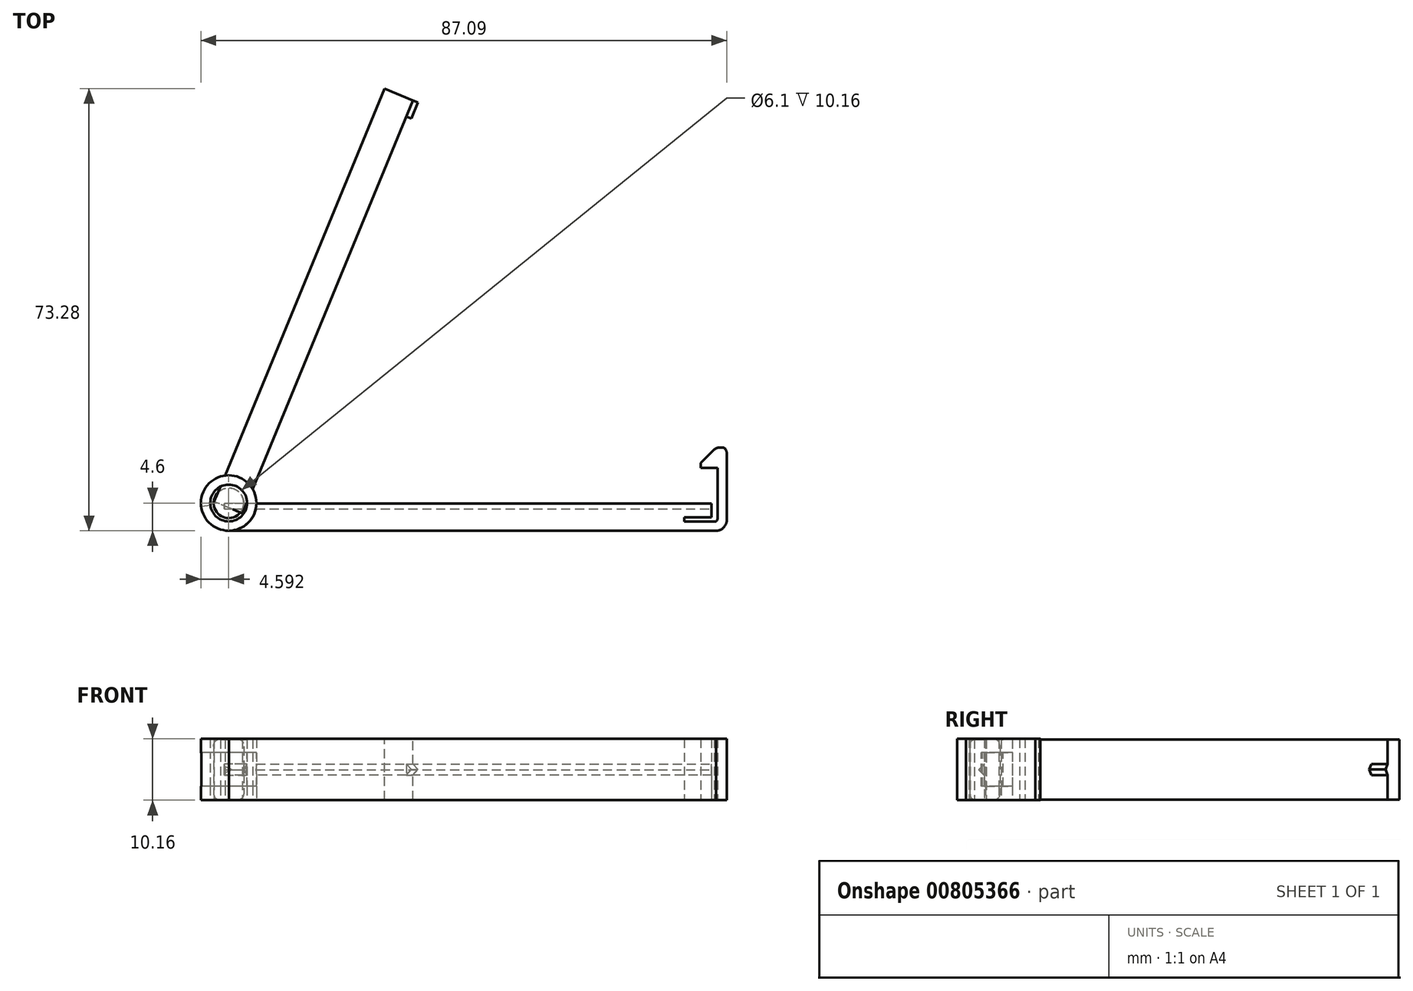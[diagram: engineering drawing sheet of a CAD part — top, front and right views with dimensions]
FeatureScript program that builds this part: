
annotation { "Feature Type Name" : "Feature", "Feature Type Description" : "" }
export const myFeature = defineFeature(function(context is Context, id is Id, definition is map)
    precondition{}
    {
        {
            assignVariable(context, id + "F0", {"name" : "length", "anyValue" : 1});
        }
        {
            var Q0;
            Q0=qCreatedBy(makeId("Top.planeOp"),FACE);
            var sketch = newSketch(context, id + "F1", { "sketchPlane" : qUnion([Q0])});
            skPoint(sketch, "E0", {"position": v(-38.94, -27.75) * mm});
            skCircle(sketch, "E1", {"center": v(-38.94, -27.75) * mm, "radius": 2.5 * mm});
            skLineSegment(sketch, "E2", {"start": v(-40.72, -25.98) * mm, "end": v(-38.24, -19.97) * mm});
            skLineSegment(sketch, "E3", {"start": v(14.08, 32.35) * mm, "end": v(17.62, 28.81) * mm});
            skLineSegment(sketch, "E4", {"start": v(-34.78, -23.44) * mm, "end": v(-33.99, -24.23) * mm});
            skLineSegment(sketch, "E5", {"start": v(-33.99, -24.23) * mm, "end": v(18.32, 28.1) * mm});
            skLineSegment(sketch, "E6", {"start": v(18.32, 28.1) * mm, "end": v(17.62, 28.81) * mm});
            skLineSegment(sketch, "E7", {"start": v(-40.72, -25.98) * mm, "end": v(-38.94, -27.75) * mm});
            skLineSegment(sketch, "E8", {"start": v(-37.25, -25.9) * mm, "end": v(-38.94, -27.75) * mm});
            skLineSegment(sketch, "E9", {"start": v(-38.24, -19.97) * mm, "end": v(-34.78, -23.44) * mm});
            skPoint(sketch, "E10", {"position": v(-38.24, -19.97) * mm});
            skLineSegment(sketch, "E11", {"start": v(-38.24, -19.97) * mm, "end": v(-38.24, -19.97) * mm});
            skLineSegment(sketch, "E12", {"start": v(-38.24, -19.97) * mm, "end": v(14.08, 32.35) * mm});
            skLineSegment(sketch, "E13", {"start": v(-37.25, -25.9) * mm, "end": v(-34.78, -23.44) * mm});
            skLineSegment(sketch, "E14", {"start": v(-34.78, -23.44) * mm, "end": v(17.62, 28.81) * mm});
            skSolve(sketch);
        }
        {
            var Q0;
            {var subQ0=sQuery(id+"F1.wireOp",EDGE,"E7");Q0=makeQuery(id+"F1.imprint","IMPRINT",FACE,{"disambiguationData":[TD([[makeQuery(id+"F1.imprint","IMPRINT",EDGE,{"derivedFrom":subQ0}),-1.0]])]});}
            var Q1;
            {var subQ0=sQuery(id+"F1.wireOp",EDGE,"E7");Q1=makeQuery(id+"F1.imprint","IMPRINT",FACE,{"disambiguationData":[TD([[makeQuery(id+"F1.imprint","IMPRINT",EDGE,{"derivedFrom":subQ0}),1.0]])]});}
            var Q2;
            Q2=sQuery(id+"F1.wireOp",EDGE,"E1");
            extrude(context, id + "F2", {"entities" : qUnion([Q0, Q1]), "surfaceEntities" : qUnion([Q2]), "endBound" : BoundingType.SYMMETRIC, "depth" : 10.16 * mm, "offsetDistance" : 25.4 * mm, "hasSecondDirection" : true, "secondDirectionOppositeDirection" : true, "secondDirectionDepth" : 5.08 * mm});
        }
        {
            var Q0;
            {var subQ0=sQuery(id+"F1.wireOp",EDGE,"E2");Q0=makeQuery(id+"F1.imprint","IMPRINT",FACE,{"disambiguationData":[TD([[makeQuery(id+"F1.imprint","IMPRINT",EDGE,{"derivedFrom":subQ0}),-1.0]])]});}
            var Q1;
            Q1=sQuery(id+"F1.wireOp",EDGE,"E2");
            var Q2;
            Q2=sQuery(id+"F1.wireOp",EDGE,"E7");
            var Q3;
            Q3=sQuery(id+"F1.wireOp",EDGE,"E8");
            var Q4;
            Q4=sQuery(id+"F1.wireOp",EDGE,"E13");
            var Q5;
            Q5=sQuery(id+"F1.wireOp",EDGE,"E9");
            var Q6;
            Q6=sQuery(id+"F1.wireOp",EDGE,"E11");
            extrude(context, id + "F3", {"entities" : qUnion([Q0]), "surfaceEntities" : qUnion([Q1, Q2, Q3, Q4, Q5, Q6]), "depth" : 2.54 * mm, "offsetDistance" : 25.4 * mm, "hasSecondDirection" : true, "secondDirectionOppositeDirection" : true, "secondDirectionDepth" : 2.54 * mm});
        }
        {
            var Q0;
            Q0=makeQuery(id+"F3.opExtrude","SWEPT_FACE",FACE,{"disambiguationData":[OSD([sQuery(id+"F1.wireOp",EDGE,"E2")])]});
            cPlane(context, id + "F4", {"entities" : qUnion([Q0]), "cplaneType" : CPlaneType.OFFSET, "offset" : 0 * mm, "width" : 152.4 * mm, "height" : 152.4 * mm});
        }
        {
            var Q0;
            Q0=qCreatedBy(id+"F4.planeOp",FACE);
            var sketch = newSketch(context, id + "F5", { "sketchPlane" : qUnion([Q0])});
            skLineSegment(sketch, "E15", {"start": v(-32.83, 2.46) * mm, "end": v(-32.83, 4.98) * mm});
            skLineSegment(sketch, "E16", {"start": v(-32.83, 4.98) * mm, "end": v(41.22, 4.98) * mm});
            skLineSegment(sketch, "E17", {"start": v(41.22, 4.98) * mm, "end": v(41.22, -5.01) * mm});
            skLineSegment(sketch, "E18", {"start": v(-32.83, -5.01) * mm, "end": v(-32.83, -2.49) * mm});
            skLineSegment(sketch, "E19", {"start": v(-32.83, -2.49) * mm, "end": v(-32.83, 2.46) * mm});
            skLineSegment(sketch, "E20", {"start": v(41.22, -5.01) * mm, "end": v(-32.83, -5.01) * mm});
            skSolve(sketch);
        }
        {
            var Q0;
            Q0=makeQuery(id+"F5.imprint","IMPRINT",FACE,{"disambiguationData":[TD([[makeQuery(id+"F5.imprint","IMPRINT",EDGE,{"derivedFrom":sQuery(id+"F5.wireOp",EDGE,"E15")}),-1.0]])]});
            var Q1;
            Q1=sQuery(id+"F5.wireOp",EDGE,"eYhi1MpS-VNJ7-cJgw-dw6u-FeKjFtGwhdby");
            var Q2;
            Q2=sQuery(id+"F5.wireOp",EDGE,"9ZvoHkQc-CYR2-l6kY-dSE9-MnJMkJ3q8TrI");
            var Q3;
            Q3=sQuery(id+"F5.wireOp",EDGE,"f5ExaPfC-bsAL-oc1X-y0ir-NheHorUjfFg7");
            var Q4;
            Q4=sQuery(id+"F5.wireOp",EDGE,"FQlkaopt-CBbH-tw7l-wL5q-EB0wirjKs65a");
            var Q5;
            Q5=sQuery(id+"F5.wireOp",EDGE,"TvMCOCRa-EXjV-ulm1-JOX4-v2cfaanY2Bvr");
            var Q6;
            Q6=sQuery(id+"F5.wireOp",EDGE,"lmaLCBwB-aZ1K-e3RN-zV7k-oPSpfsVAcoc8");
            extrude(context, id + "F6", {"entities" : qUnion([Q0]), "surfaceEntities" : qUnion([Q1, Q2, Q3, Q4, Q5, Q6]), "oppositeDirection" : true, "depth" : 5.08 * mm, "offsetDistance" : 25.4 * mm});
        }
        {
            var Q0;
            Q0=makeQuery(id+"F6.opExtrude","SWEPT_FACE",FACE,{"disambiguationData":[OSD([sQuery(id+"F5.wireOp",EDGE,"E15"),sQuery(id+"F5.wireOp",EDGE,"E18"),sQuery(id+"F5.wireOp",EDGE,"E19")])]});
            cPlane(context, id + "F7", {"entities" : qUnion([Q0]), "cplaneType" : CPlaneType.OFFSET, "offset" : 0 * mm, "width" : 152.4 * mm, "height" : 152.4 * mm});
        }
        {
            var Q0;
            Q0=qCreatedBy(id+"F7.planeOp",FACE);
            var sketch = newSketch(context, id + "F8", { "sketchPlane" : qUnion([Q0])});
            skLineSegment(sketch, "E21", {"start": v(22.65, -0.93) * mm, "end": v(21.75, 0) * mm});
            skLineSegment(sketch, "E22", {"start": v(21.75, 0) * mm, "end": v(22.65, 0.92) * mm});
            skLineSegment(sketch, "E23", {"start": v(22.65, 0.92) * mm, "end": v(22.65, -0.93) * mm});
            skSolve(sketch);
        }
        {
            var Q0;
            Q0=makeQuery(id+"F8.imprint","IMPRINT",FACE,{"disambiguationData":[TD([[makeQuery(id+"F8.imprint","IMPRINT",EDGE,{"derivedFrom":sQuery(id+"F8.wireOp",EDGE,"E21")}),-1.0]])]});
            extrude(context, id + "F9", {"entities" : qUnion([Q0]), "operationType" : NewBodyOperationType.ADD, "oppositeDirection" : true, "depth" : (getVariable(context, 'length') * 2.92) * mm, "offsetDistance" : 25.4 * mm});
        }
        {
            var Q0;
            Q0=makeQuery(id+"F2.opExtrude","CAP_FACE",FACE,{"disambiguationData":[OSD([sQuery(id+"F1.wireOp",EDGE,"E1"),sQuery(id+"F1.wireOp",EDGE,"E2")])],"isStart":false});
            var Q1;
            Q1=makeQuery(id+"F2.opExtrude","CAP_FACE",FACE,{"disambiguationData":[OSD([sQuery(id+"F1.wireOp",EDGE,"E1"),sQuery(id+"F1.wireOp",EDGE,"E2")])],"isStart":true});
            fillet(context, id + "F10", {"entities" : qUnion([Q0, Q1]), "radius" : 1.27 * mm, "tangentPropagation" : true, "rho" : 0.5, "crossSection" : FilletCrossSection.CONIC, "allowEdgeOverflow" : false});
        }
        {
            var Q0;
            Q0=qCreatedBy(makeId("Top.planeOp"),FACE);
            var sketch = newSketch(context, id + "F11", { "sketchPlane" : qUnion([Q0])});
            skLineSegment(sketch, "E24", {"start": v(-34.35, -27.85) * mm, "end": v(41.05, -27.85) * mm});
            skLineSegment(sketch, "E25", {"start": v(41.05, -27.85) * mm, "end": v(41.05, -30.15) * mm});
            skLineSegment(sketch, "E26", {"start": v(41.05, -30.15) * mm, "end": v(36.53, -30.15) * mm});
            skLineSegment(sketch, "E27", {"start": v(36.53, -30.15) * mm, "end": v(36.53, -30.85) * mm});
            skLineSegment(sketch, "E28", {"start": v(36.53, -30.85) * mm, "end": v(41.54, -30.85) * mm});
            skLineSegment(sketch, "E29", {"start": v(42.04, -30.34) * mm, "end": v(42.04, -21.96) * mm});
            skLineSegment(sketch, "E30", {"start": v(42.04, -21.96) * mm, "end": v(39.27, -21.96) * mm});
            skLineSegment(sketch, "E31", {"start": v(39.27, -21.96) * mm, "end": v(39.27, -21.1) * mm});
            skLineSegment(sketch, "E32", {"start": v(39.27, -21.1) * mm, "end": v(41.51, -18.9) * mm});
            skLineSegment(sketch, "E33", {"start": v(43.55, -19.35) * mm, "end": v(43.55, -30.85) * mm});
            skLineSegment(sketch, "E34", {"start": v(41.83, -32.35) * mm, "end": v(-38.91, -32.34) * mm});
            skFitSpline(sketch, "E35", {"points": [v(42.04, -30.34) * mm, v(41.96, -30.64) * mm, v(41.76, -30.81) * mm, v(41.54, -30.85) * mm], "startDerivative": vector(-0.13, -0.89) * mm, "endDerivative": vector(-0.72, -0.04) * mm});
            skPoint(sketch, "E36", {"position": v(-38.95, -27.75) * mm});
            skCircle(sketch, "E37", {"center": v(-38.95, -27.75) * mm, "radius": 4.6 * mm});
            skCircle(sketch, "E38", {"center": v(-38.95, -27.75) * mm, "radius": 3.05 * mm});
            skArc(sketch, "E39", {"start": v(-38.91, -32.34) * mm, "mid": v(-35.71, -31.03) * mm, "end": v(-34.35, -27.85) * mm});
            skFitSpline(sketch, "E40", {"points": [v(43.55, -30.85) * mm, v(43.45, -31.19) * mm, v(43.33, -31.44) * mm, v(43.1, -31.76) * mm, v(42.8, -32.03) * mm, v(42.4, -32.24) * mm, v(42.09, -32.32) * mm, v(41.83, -32.35) * mm], "startDerivative": vector(-0.54, -2.5) * mm, "endDerivative": vector(-2.03, -0.25) * mm});
            skFitSpline(sketch, "E41", {"points": [v(41.51, -18.9) * mm, v(41.69, -18.75) * mm, v(41.95, -18.62) * mm, v(42.21, -18.56) * mm, v(42.5, -18.55) * mm, v(42.89, -18.56) * mm, v(43.11, -18.63) * mm, v(43.3, -18.76) * mm, v(43.4, -18.87) * mm, v(43.5, -19.05) * mm, v(43.54, -19.2) * mm, v(43.55, -19.35) * mm], "startDerivative": vector(1.84, 1.62) * mm, "endDerivative": vector(0.1, -3.66) * mm});
            skLineSegment(sketch, "E42", {"start": v(41.05, -30.85) * mm, "end": v(41.05, -32.35) * mm});
            skCircle(sketch, "E43", {"center": v(-38.91, -27.78) * mm, "radius": 79.98 * mm, "construction": true});
            skLineSegment(sketch, "E44", {"start": v(-34.35, -27.85) * mm, "end": v(-35.9, -27.83) * mm});
            skLineSegment(sketch, "E45", {"start": v(-41.97, -28.16) * mm, "end": v(-43.5, -28.35) * mm});
            skSolve(sketch);
        }
        {
            var Q0;
            Q0=makeQuery(id+"F11.imprint","IMPRINT",FACE,{"disambiguationData":[TD([[makeQuery(id+"F11.imprint","IMPRINT",EDGE,{"derivedFrom":sQuery(id+"F11.wireOp",EDGE,"E24")}),-1.0]])]});
            var Q1;
            Q1=sQuery(id+"F11.wireOp",EDGE,"E39");
            var Q2;
            Q2=sQuery(id+"F11.wireOp",EDGE,"E24");
            var Q3;
            Q3=sQuery(id+"F11.wireOp",EDGE,"E25");
            var Q4;
            Q4=sQuery(id+"F11.wireOp",EDGE,"E26");
            var Q5;
            Q5=sQuery(id+"F11.wireOp",EDGE,"E27");
            var Q6;
            Q6=sQuery(id+"F11.wireOp",EDGE,"E28");
            var Q7;
            Q7=sQuery(id+"F11.wireOp",EDGE,"E35");
            var Q8;
            Q8=sQuery(id+"F11.wireOp",EDGE,"E29");
            var Q9;
            Q9=sQuery(id+"F11.wireOp",EDGE,"E30");
            var Q10;
            Q10=sQuery(id+"F11.wireOp",EDGE,"E31");
            var Q11;
            Q11=sQuery(id+"F11.wireOp",EDGE,"E32");
            var Q12;
            Q12=sQuery(id+"F11.wireOp",EDGE,"E41");
            var Q13;
            Q13=sQuery(id+"F11.wireOp",EDGE,"E33");
            var Q14;
            Q14=sQuery(id+"F11.wireOp",EDGE,"E40");
            var Q15;
            Q15=sQuery(id+"F11.wireOp",EDGE,"E34");
            extrude(context, id + "F12", {"entities" : qUnion([Q0]), "surfaceEntities" : qUnion([Q1, Q2, Q3, Q4, Q5, Q6, Q7, Q8, Q9, Q10, Q11, Q12, Q13, Q14, Q15]), "depth" : 5.08 * mm, "offsetDistance" : 25.4 * mm, "hasSecondDirection" : true, "secondDirectionOppositeDirection" : true, "secondDirectionDepth" : 5.08 * mm});
        }
        {
            var Q0;
            Q0=makeQuery(id+"F12.opExtrude","SWEPT_FACE",FACE,{"disambiguationData":[OSD([sQuery(id+"F11.wireOp",EDGE,"E25")])]});
            var sketch = newSketch(context, id + "F13", { "sketchPlane" : qUnion([Q0])});
            skLineSegment(sketch, "E46", {"start": v(-24.24, 0) * mm, "end": v(-33.92, 0) * mm, "construction": true});
            skLineSegment(sketch, "E47", {"start": v(-27.85, -0.96) * mm, "end": v(-28.75, -0.03) * mm});
            skLineSegment(sketch, "E48", {"start": v(-28.75, -0.03) * mm, "end": v(-27.85, 0.89) * mm});
            skLineSegment(sketch, "E49", {"start": v(-27.85, 0.89) * mm, "end": v(-27.85, -0.96) * mm});
            skSolve(sketch);
        }
        {
            var Q0;
            Q0=makeQuery(id+"F13.imprint","IMPRINT",FACE,{"disambiguationData":[TD([[makeQuery(id+"F13.imprint","IMPRINT",EDGE,{"derivedFrom":sQuery(id+"F13.wireOp",EDGE,"E47")}),-1.0]])]});
            extrude(context, id + "F14", {"entities" : qUnion([Q0]), "operationType" : NewBodyOperationType.REMOVE, "oppositeDirection" : true, "depth" : getVariable(context, 'length') * 80.72 * mm, "offsetDistance" : 25.4 * mm});
        }
        {
            var Q0;
            Q0=makeQuery(id+"F11.imprint","IMPRINT",FACE,{"disambiguationData":[TD([[makeQuery(id+"F11.imprint","IMPRINT",EDGE,{"derivedFrom":sQuery(id+"F11.wireOp",EDGE,"E29")}),-1.0]])]});
            extrude(context, id + "F15", {"entities" : qUnion([Q0]), "operationType" : NewBodyOperationType.ADD, "depth" : 5.08 * mm, "offsetDistance" : 25.4 * mm, "hasSecondDirection" : true, "secondDirectionOppositeDirection" : true, "secondDirectionDepth" : 5.08 * mm});
        }
        {
            var Q0;
            Q0=makeQuery(id+"F11.imprint","IMPRINT",FACE,{"disambiguationData":[TD([[makeQuery(id+"F11.imprint","IMPRINT",EDGE,{"derivedFrom":sQuery(id+"F11.wireOp",EDGE,"E38")}),-1.0]])]});
            var Q1;
            {var subQ0=sQuery(id+"F11.wireOp",EDGE,"E44");Q1=makeQuery(id+"F11.imprint","IMPRINT",FACE,{"disambiguationData":[TD([[makeQuery(id+"F11.imprint","IMPRINT",EDGE,{"derivedFrom":subQ0}),1.0]])]});}
            extrude(context, id + "F16", {"entities" : qUnion([Q0, Q1]), "operationType" : NewBodyOperationType.ADD, "endBound" : BoundingType.SYMMETRIC, "depth" : 10.16 * mm, "offsetDistance" : 25.4 * mm});
        }
        {
            var Q0;
            Q0=makeQuery(id+"F11.imprint","IMPRINT",FACE,{"disambiguationData":[TD([[makeQuery(id+"F11.imprint","IMPRINT",EDGE,{"derivedFrom":sQuery(id+"F11.wireOp",EDGE,"E38")}),-1.0]])]});
            extrude(context, id + "F17", {"entities" : qUnion([Q0]), "operationType" : NewBodyOperationType.REMOVE, "endBound" : BoundingType.SYMMETRIC, "oppositeDirection" : true, "depth" : 5.6 * mm, "offsetDistance" : 25.4 * mm});
        }
    });
